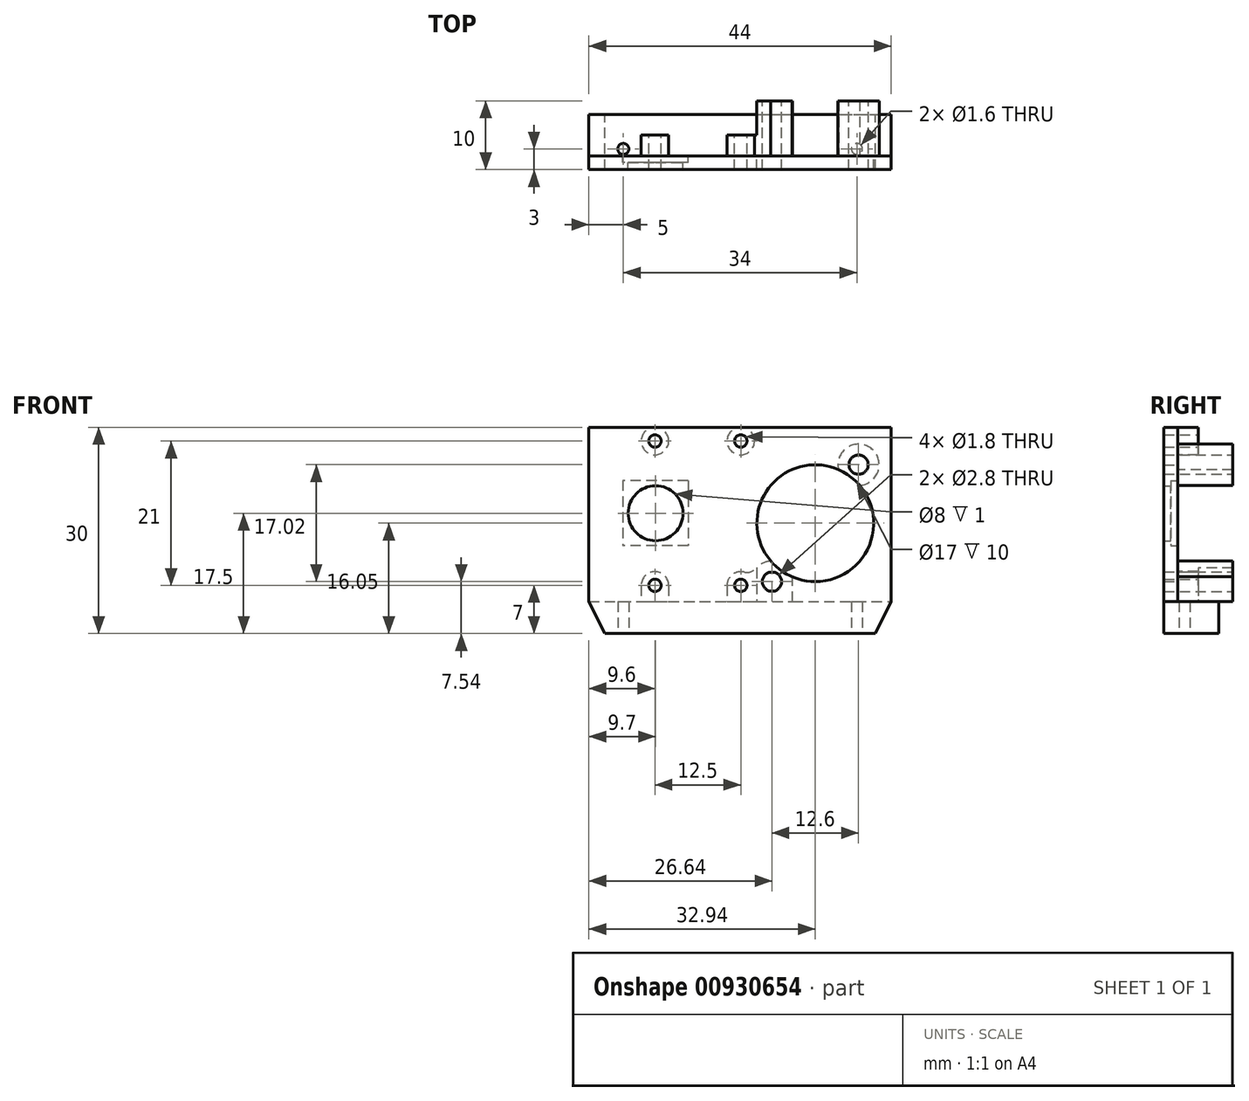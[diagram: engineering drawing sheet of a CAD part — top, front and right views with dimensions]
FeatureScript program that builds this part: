
annotation { "Feature Type Name" : "Feature", "Feature Type Description" : "" }
export const myFeature = defineFeature(function(context is Context, id is Id, definition is map)
    precondition{}
    {
        {
            var Q0;
            Q0=qCreatedBy(makeId("Front.planeOp"),FACE);
            var sketch = newSketch(context, id + "F0", { "sketchPlane" : qUnion([Q0])});
            skLineSegment(sketch, "E0", {"start": v(-22.5, 0) * mm, "end": v(22.5, 0) * mm, "construction": true});
            skLineSegment(sketch, "E1", {"start": v(-20, -5) * mm, "end": v(20, -5) * mm, "construction": true});
            skLineSegment(sketch, "E2", {"start": v(20, -5) * mm, "end": v(22.5, 0) * mm, "construction": true});
            skLineSegment(sketch, "E3", {"start": v(-22.5, 0) * mm, "end": v(-20, -5) * mm, "construction": true});
            skLineSegment(sketch, "E4.bottom", {"start": v(2.1, 22.6) * mm, "end": v(22, 22.6) * mm, "construction": true});
            skLineSegment(sketch, "E4.top", {"start": v(2.1, 0.5) * mm, "end": v(22, 0.5) * mm, "construction": true});
            skLineSegment(sketch, "E4.left", {"start": v(2.1, 22.6) * mm, "end": v(2.1, 0.5) * mm, "construction": true});
            skLineSegment(sketch, "E4.right", {"start": v(22, 22.6) * mm, "end": v(22, 0.5) * mm, "construction": true});
            skLineSegment(sketch, "E5.bottom", {"start": v(-19.76, 25.5) * mm, "end": v(0.1, 25.5) * mm, "construction": true});
            skLineSegment(sketch, "E5.top", {"start": v(-19.76, 0.5) * mm, "end": v(0.1, 0.5) * mm, "construction": true});
            skLineSegment(sketch, "E5.left", {"start": v(-21.76, 23.5) * mm, "end": v(-21.76, 2.5) * mm, "construction": true});
            skLineSegment(sketch, "E5.right", {"start": v(2.1, 23.5) * mm, "end": v(2.1, 2.5) * mm, "construction": true});
            skArc(sketch, "E6", {"start": v(-19.76, 25.5) * mm, "mid": v(-21.18, 24.91) * mm, "end": v(-21.76, 23.5) * mm, "construction": true});
            skArc(sketch, "E7", {"start": v(2.1, 23.5) * mm, "mid": v(1.51, 24.91) * mm, "end": v(0.1, 25.5) * mm, "construction": true});
            skArc(sketch, "E8", {"start": v(-21.76, 2.5) * mm, "mid": v(-21.18, 1.09) * mm, "end": v(-19.76, 0.5) * mm, "construction": true});
            skArc(sketch, "E9", {"start": v(0.1, 0.5) * mm, "mid": v(1.51, 1.09) * mm, "end": v(2.1, 2.5) * mm, "construction": true});
            skCircle(sketch, "E10", {"center": v(-12.4, 23.5) * mm, "radius": 1.1 * mm, "construction": true});
            skCircle(sketch, "E11", {"center": v(-12.4, 2.5) * mm, "radius": 1.1 * mm, "construction": true});
            skCircle(sketch, "E12", {"center": v(0.1, 2.5) * mm, "radius": 1.1 * mm, "construction": true});
            skCircle(sketch, "E13", {"center": v(0.1, 23.5) * mm, "radius": 1.1 * mm, "construction": true});
            skLineSegment(sketch, "E14", {"start": v(-12.4, 23.5) * mm, "end": v(0.1, 23.5) * mm, "construction": true});
            skLineSegment(sketch, "E15", {"start": v(-12.4, 23.5) * mm, "end": v(-12.4, 2.5) * mm, "construction": true});
            skCircle(sketch, "E16", {"center": v(10.94, 11.55) * mm, "radius": 8.2 * mm, "construction": true});
            skCircle(sketch, "E17", {"center": v(17.24, 20.06) * mm, "radius": 1.55 * mm, "construction": true});
            skCircle(sketch, "E18", {"center": v(4.64, 3.04) * mm, "radius": 1.55 * mm, "construction": true});
            skLineSegment(sketch, "E19.bottom", {"start": v(-16.55, 17.25) * mm, "end": v(-8.05, 17.25) * mm, "construction": true});
            skLineSegment(sketch, "E19.top", {"start": v(-16.55, 8.75) * mm, "end": v(-8.05, 8.75) * mm, "construction": true});
            skLineSegment(sketch, "E19.left", {"start": v(-16.55, 17.25) * mm, "end": v(-16.55, 8.75) * mm, "construction": true});
            skLineSegment(sketch, "E19.right", {"start": v(-8.05, 17.25) * mm, "end": v(-8.05, 8.75) * mm, "construction": true});
            skCircle(sketch, "E20", {"center": v(-12.3, 13) * mm, "radius": 3.7 * mm, "construction": true});
            skCircle(sketch, "E21", {"center": v(20.8, 17.44) * mm, "radius": 0.5 * mm, "construction": true});
            skCircle(sketch, "E22", {"center": v(20.8, 14.9) * mm, "radius": 0.5 * mm, "construction": true});
            skLineSegment(sketch, "E23", {"start": v(20.8, 17.44) * mm, "end": v(20.8, 2.2) * mm, "construction": true});
            skCircle(sketch, "E24", {"center": v(20.8, 12.36) * mm, "radius": 0.5 * mm, "construction": true});
            skCircle(sketch, "E25", {"center": v(20.8, 9.82) * mm, "radius": 0.5 * mm, "construction": true});
            skCircle(sketch, "E26", {"center": v(20.8, 7.28) * mm, "radius": 0.5 * mm, "construction": true});
            skCircle(sketch, "E27", {"center": v(20.8, 4.74) * mm, "radius": 0.5 * mm, "construction": true});
            skCircle(sketch, "E28", {"center": v(20.8, 2.2) * mm, "radius": 0.5 * mm, "construction": true});
            skSolve(sketch);
        }
        {
            var Q0;
            Q0=qCreatedBy(makeId("Front.planeOp"),FACE);
            var sketch = newSketch(context, id + "F1", { "sketchPlane" : qUnion([Q0])});
            skLineSegment(sketch, "E29", {"start": v(-22, 0.12) * mm, "end": v(-19.7, -4.5) * mm});
            skLineSegment(sketch, "E30", {"start": v(-19.7, -4.5) * mm, "end": v(19.7, -4.5) * mm});
            skLineSegment(sketch, "E31", {"start": v(19.7, -4.5) * mm, "end": v(22, 0.12) * mm});
            skLineSegment(sketch, "E32", {"start": v(-22, 0.12) * mm, "end": v(-22, 25.5) * mm});
            skLineSegment(sketch, "E33", {"start": v(-22, 25.5) * mm, "end": v(22, 25.5) * mm});
            skLineSegment(sketch, "E34", {"start": v(22, 25.5) * mm, "end": v(22, 0.12) * mm});
            skCircle(sketch, "E35", {"center": v(-12.3, 13) * mm, "radius": 4 * mm});
            skCircle(sketch, "E36", {"center": v(10.94, 11.55) * mm, "radius": 8.5 * mm});
            skSolve(sketch);
        }
        {
            var Q0;
            Q0=qSketchRegion(id+"F1",true);
            extrude(context, id + "F2", {"entities" : qUnion([Q0]), "depth" : 2 * mm, "offsetDistance" : 25 * mm});
        }
        {
            var Q0;
            Q0=makeQuery(id+"F2.opExtrude","CAP_FACE",FACE,{"disambiguationData":[OSD([sQuery(id+"F1.wireOp",EDGE,"E29"),sQuery(id+"F1.wireOp",EDGE,"E30"),sQuery(id+"F1.wireOp",EDGE,"E31"),sQuery(id+"F1.wireOp",EDGE,"E32"),sQuery(id+"F1.wireOp",EDGE,"E33"),sQuery(id+"F1.wireOp",EDGE,"E34"),sQuery(id+"F1.wireOp",EDGE,"E35"),sQuery(id+"F1.wireOp",EDGE,"E36")])],"isStart":true});
            var sketch = newSketch(context, id + "F3", { "sketchPlane" : qUnion([Q0])});
            skLineSegment(sketch, "E37", {"start": v(-22, 0.12) * mm, "end": v(-19.7, -4.5) * mm});
            skLineSegment(sketch, "E38", {"start": v(-19.7, -4.5) * mm, "end": v(19.7, -4.5) * mm});
            skLineSegment(sketch, "E39", {"start": v(19.7, -4.5) * mm, "end": v(22, 0.12) * mm});
            skLineSegment(sketch, "E40", {"start": v(22, 0.12) * mm, "end": v(-22, 0.12) * mm});
            skSolve(sketch);
        }
        {
            var Q0;
            Q0=qSketchRegion(id+"F3",true);
            extrude(context, id + "F4", {"entities" : qUnion([Q0]), "operationType" : NewBodyOperationType.ADD, "depth" : 6 * mm, "offsetDistance" : 25 * mm});
        }
        {
            var Q0;
            Q0=makeQuery(id+"F4.boolean.opBoolean","MERGE",FACE,{"derivedFrom":[makeQuery(id+"F2.opExtrude","SWEPT_FACE",FACE,{"disambiguationData":[OSD([sQuery(id+"F1.wireOp",EDGE,"E30")])]}),makeQuery(id+"F4.opExtrude","SWEPT_FACE",FACE,{"disambiguationData":[OSD([sQuery(id+"F3.wireOp",EDGE,"E38")])]})]});
            var sketch = newSketch(context, id + "F5", { "sketchPlane" : qUnion([Q0])});
            skCircle(sketch, "E41", {"center": v(-17, -1) * mm, "radius": 0.8 * mm});
            skCircle(sketch, "E42", {"center": v(17, -1) * mm, "radius": 0.8 * mm});
            skSolve(sketch);
        }
        {
            var Q0;
            Q0=qSketchRegion(id+"F5",true);
            extrude(context, id + "F6", {"entities" : qUnion([Q0]), "operationType" : NewBodyOperationType.REMOVE, "endBound" : BoundingType.UP_TO_NEXT, "oppositeDirection" : true, "depth" : 25 * mm, "offsetDistance" : 25 * mm});
        }
        {
            var Q0;
            Q0=makeQuery(id+"F2.opExtrude","CAP_FACE",FACE,{"disambiguationData":[OSD([sQuery(id+"F1.wireOp",EDGE,"E29"),sQuery(id+"F1.wireOp",EDGE,"E30"),sQuery(id+"F1.wireOp",EDGE,"E31"),sQuery(id+"F1.wireOp",EDGE,"E32"),sQuery(id+"F1.wireOp",EDGE,"E33"),sQuery(id+"F1.wireOp",EDGE,"E34"),sQuery(id+"F1.wireOp",EDGE,"E35"),sQuery(id+"F1.wireOp",EDGE,"E36")])],"isStart":true});
            var sketch = newSketch(context, id + "F7", { "sketchPlane" : qUnion([Q0])});
            skArc(sketch, "E43", {"start": v(-14.33, 19.35) * mm, "mid": v(-19.03, 22.47) * mm, "end": v(-17.4, 17.06) * mm});
            skArc(sketch, "E44", {"start": v(-7.55, 3.75) * mm, "mid": v(-7.62, 3.4) * mm, "end": v(-7.64, 3.04) * mm});
            skArc(sketch, "E45", {"start": v(-14.33, 19.35) * mm, "mid": v(-16, 18.38) * mm, "end": v(-17.4, 17.06) * mm});
            skArc(sketch, "E46", {"start": v(-7.55, 3.75) * mm, "mid": v(-5.88, 4.72) * mm, "end": v(-4.47, 6.04) * mm});
            skLineSegment(sketch, "E47", {"start": v(-2.4, 5.04) * mm, "end": v(-2.4, 0.12) * mm});
            skLineSegment(sketch, "E48", {"start": v(-7.64, 0.12) * mm, "end": v(-2.4, 0.12) * mm});
            skLineSegment(sketch, "E49", {"start": v(-7.64, 0.12) * mm, "end": v(-7.64, 3.04) * mm});
            skArc(sketch, "E50.trimOffspring", {"start": v(-2.4, 5.04) * mm, "mid": v(-3.34, 5.74) * mm, "end": v(-4.47, 6.04) * mm});
            skSolve(sketch);
        }
        {
            var Q0;
            Q0=qSketchRegion(id+"F7",true);
            extrude(context, id + "F8", {"entities" : qUnion([Q0]), "operationType" : NewBodyOperationType.ADD, "depth" : 8 * mm, "offsetDistance" : 25 * mm});
        }
        {
            var Q0;
            Q0=makeQuery(id+"F8.opExtrude","CAP_FACE",FACE,{"disambiguationData":[OSD([sQuery(id+"F7.wireOp",EDGE,"E43"),sQuery(id+"F7.wireOp",EDGE,"E45")])],"isStart":false});
            var sketch = newSketch(context, id + "F9", { "sketchPlane" : qUnion([Q0])});
            skCircle(sketch, "E51", {"center": v(-17.24, 20.06) * mm, "radius": 1.4 * mm});
            skCircle(sketch, "E52", {"center": v(-4.64, 3.04) * mm, "radius": 1.4 * mm});
            skSolve(sketch);
        }
        {
            var Q0;
            Q0=qSketchRegion(id+"F9",true);
            extrude(context, id + "F10", {"entities" : qUnion([Q0]), "operationType" : NewBodyOperationType.REMOVE, "endBound" : BoundingType.UP_TO_NEXT, "oppositeDirection" : true, "depth" : 25 * mm, "offsetDistance" : 25 * mm});
        }
        {
            var Q0;
            Q0=makeQuery(id+"F2.opExtrude","CAP_FACE",FACE,{"disambiguationData":[OSD([sQuery(id+"F1.wireOp",EDGE,"E29"),sQuery(id+"F1.wireOp",EDGE,"E30"),sQuery(id+"F1.wireOp",EDGE,"E31"),sQuery(id+"F1.wireOp",EDGE,"E32"),sQuery(id+"F1.wireOp",EDGE,"E33"),sQuery(id+"F1.wireOp",EDGE,"E34"),sQuery(id+"F1.wireOp",EDGE,"E35"),sQuery(id+"F1.wireOp",EDGE,"E36")])],"isStart":true});
            var sketch = newSketch(context, id + "F11", { "sketchPlane" : qUnion([Q0])});
            skCircle(sketch, "E53", {"center": v(-0.1, 23.5) * mm, "radius": 2 * mm});
            skCircle(sketch, "E54", {"center": v(12.4, 23.5) * mm, "radius": 2 * mm});
            skArc(sketch, "E55", {"start": v(1.9, 2.5) * mm, "mid": v(1.14, 4.07) * mm, "end": v(-0.55, 4.45) * mm});
            skArc(sketch, "E56", {"start": v(14.4, 2.5) * mm, "mid": v(12.4, 4.5) * mm, "end": v(10.4, 2.5) * mm});
            skLineSegment(sketch, "E57", {"start": v(1.9, 2.5) * mm, "end": v(1.9, 0.12) * mm});
            skLineSegment(sketch, "E58", {"start": v(-2.4, 0.12) * mm, "end": v(1.9, 0.12) * mm});
            skLineSegment(sketch, "E59", {"start": v(10.4, 2.5) * mm, "end": v(10.4, 0.12) * mm});
            skLineSegment(sketch, "E60", {"start": v(14.4, 2.5) * mm, "end": v(14.4, 0.12) * mm});
            skLineSegment(sketch, "E61", {"start": v(10.4, 0.12) * mm, "end": v(14.4, 0.12) * mm});
            skArc(sketch, "E62", {"start": v(-2.4, 5.04) * mm, "mid": v(-1.56, 4.49) * mm, "end": v(-0.55, 4.45) * mm});
            skLineSegment(sketch, "E63", {"start": v(-2.4, 5.04) * mm, "end": v(-2.4, 0.12) * mm});
            skSolve(sketch);
        }
        {
            var Q0;
            Q0=qSketchRegion(id+"F11",true);
            extrude(context, id + "F12", {"entities" : qUnion([Q0]), "operationType" : NewBodyOperationType.ADD, "depth" : 3 * mm, "offsetDistance" : 25 * mm});
        }
        {
            var Q0;
            Q0=makeQuery(id+"F2.opExtrude","CAP_FACE",FACE,{"disambiguationData":[OSD([sQuery(id+"F1.wireOp",EDGE,"E29"),sQuery(id+"F1.wireOp",EDGE,"E30"),sQuery(id+"F1.wireOp",EDGE,"E31"),sQuery(id+"F1.wireOp",EDGE,"E32"),sQuery(id+"F1.wireOp",EDGE,"E33"),sQuery(id+"F1.wireOp",EDGE,"E34"),sQuery(id+"F1.wireOp",EDGE,"E35"),sQuery(id+"F1.wireOp",EDGE,"E36")])],"isStart":true});
            var sketch = newSketch(context, id + "F13", { "sketchPlane" : qUnion([Q0])});
            skLineSegment(sketch, "E64.bottom", {"start": v(7.55, 17.75) * mm, "end": v(17.05, 17.75) * mm});
            skLineSegment(sketch, "E64.top", {"start": v(7.55, 8.25) * mm, "end": v(17.05, 8.25) * mm});
            skLineSegment(sketch, "E64.left", {"start": v(7.55, 17.75) * mm, "end": v(7.55, 8.25) * mm});
            skLineSegment(sketch, "E64.right", {"start": v(17.05, 17.75) * mm, "end": v(17.05, 8.25) * mm});
            skCircle(sketch, "E65", {"center": v(12.3, 13) * mm, "radius": 4 * mm});
            skSolve(sketch);
        }
        {
            var Q0;
            Q0=qSketchRegion(id+"F13",true);
            extrude(context, id + "F14", {"entities" : qUnion([Q0]), "operationType" : NewBodyOperationType.REMOVE, "oppositeDirection" : true, "depth" : 1 * mm, "offsetDistance" : 25 * mm});
        }
        {
            var Q0;
            Q0=makeQuery(id+"F12.opExtrude","CAP_FACE",FACE,{"disambiguationData":[OSD([sQuery(id+"F11.wireOp",EDGE,"E53")])],"isStart":false});
            var sketch = newSketch(context, id + "F15", { "sketchPlane" : qUnion([Q0])});
            skCircle(sketch, "E66", {"center": v(-0.1, 23.5) * mm, "radius": 0.9 * mm});
            skCircle(sketch, "E67", {"center": v(12.4, 23.5) * mm, "radius": 0.9 * mm});
            skCircle(sketch, "E68", {"center": v(-0.1, 2.5) * mm, "radius": 0.9 * mm});
            skCircle(sketch, "E69", {"center": v(12.4, 2.5) * mm, "radius": 0.9 * mm});
            skSolve(sketch);
        }
        {
            var Q0;
            Q0=qSketchRegion(id+"F15",true);
            extrude(context, id + "F16", {"entities" : qUnion([Q0]), "operationType" : NewBodyOperationType.REMOVE, "endBound" : BoundingType.UP_TO_NEXT, "oppositeDirection" : true, "depth" : 25 * mm, "offsetDistance" : 25 * mm});
        }
    });
